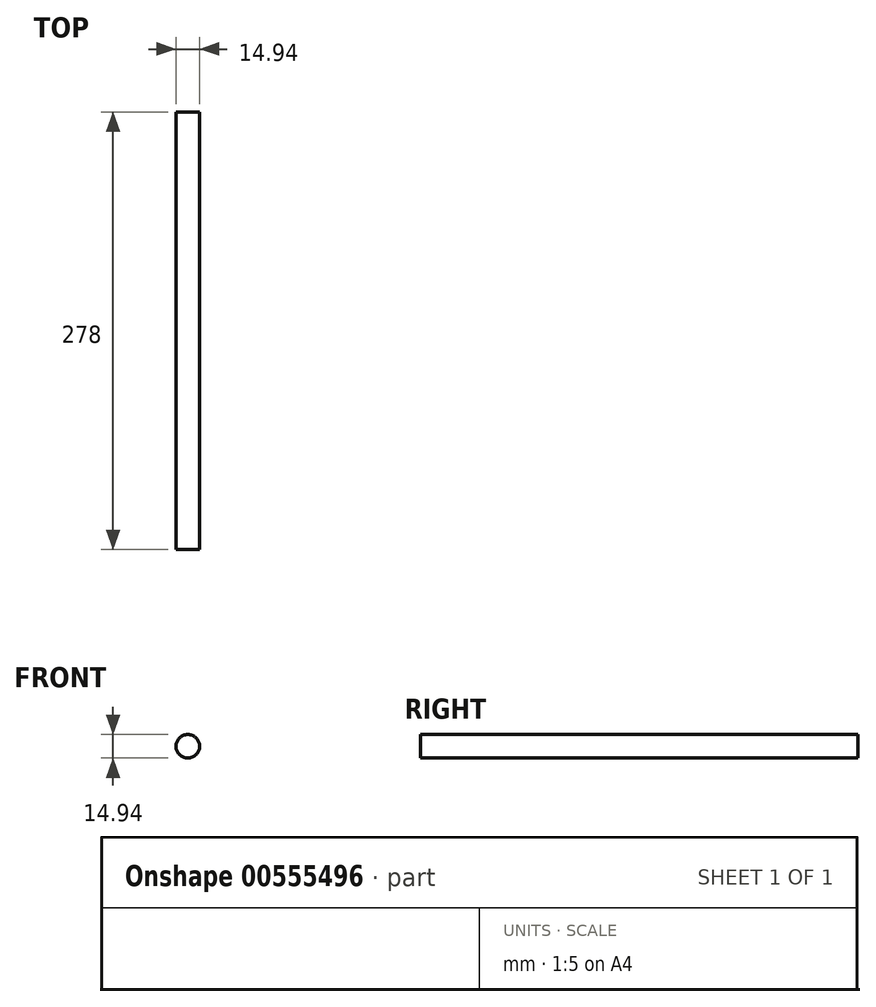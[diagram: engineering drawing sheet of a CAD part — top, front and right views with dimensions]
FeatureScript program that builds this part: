
annotation { "Feature Type Name" : "Feature", "Feature Type Description" : "" }
export const myFeature = defineFeature(function(context is Context, id is Id, definition is map)
    precondition{}
    {
        {
            var Q0;
            Q0=qCreatedBy(makeId("Front.planeOp"),FACE);
            var sketch = newSketch(context, id + "F0", { "sketchPlane" : qUnion([Q0])});
            skCircle(sketch, "E0", {"center": v(0, 0) * mm, "radius": 7.47 * mm});
            skSolve(sketch);
        }
        {
            var Q0;
            Q0 = qSketchRegion(id + "F0", true);
            extrude(context, id + "F1", {"entities" : qUnion([Q0]), "depth" : 278 * mm, "offsetDistance" : 25 * mm});
        }
    });
